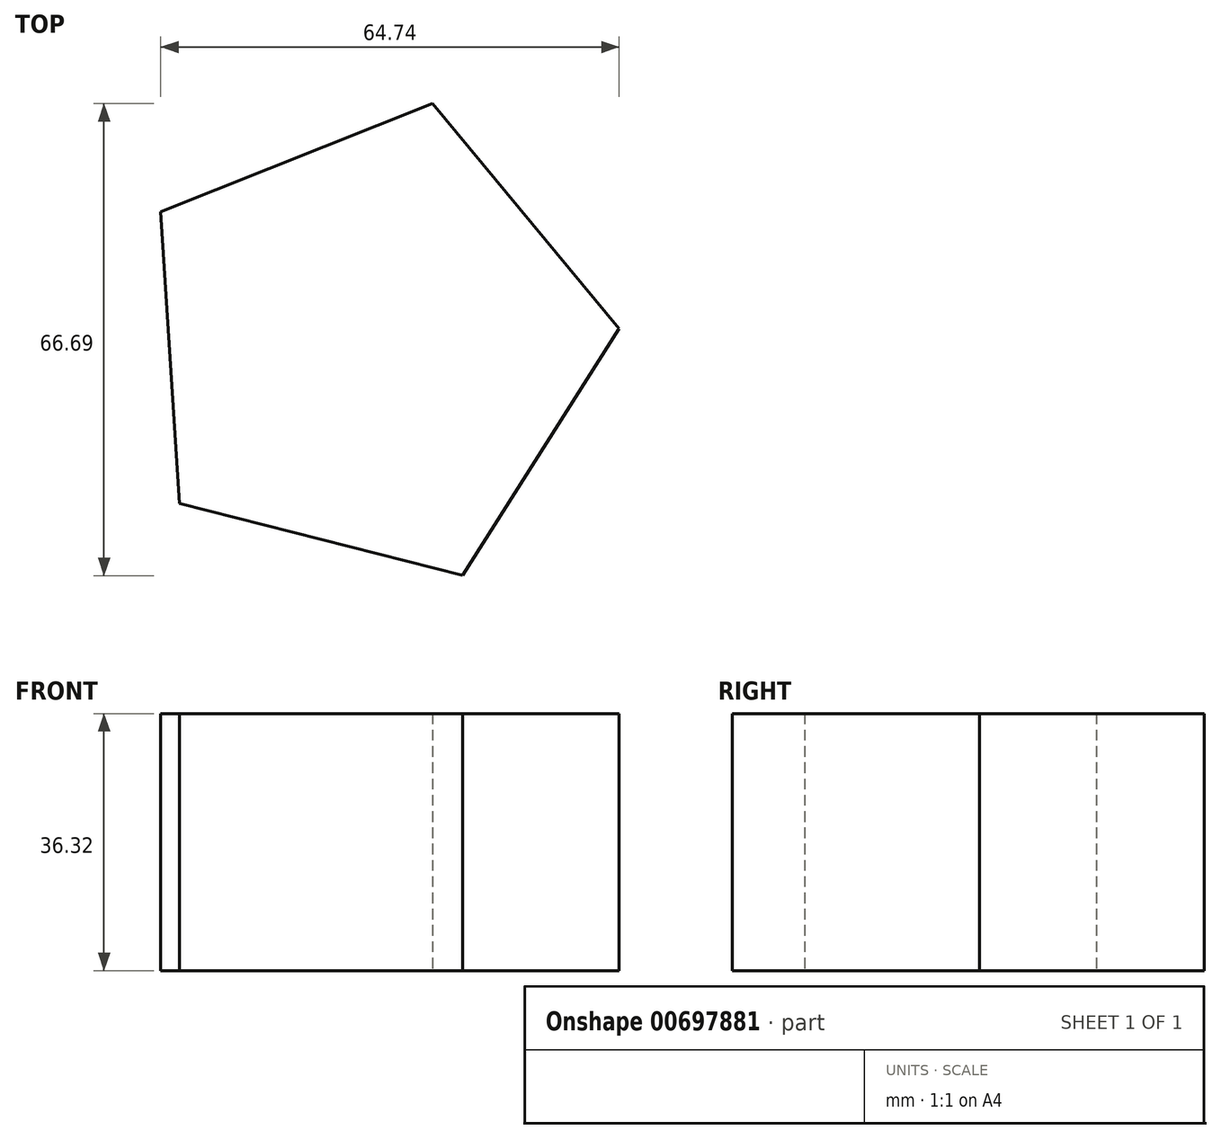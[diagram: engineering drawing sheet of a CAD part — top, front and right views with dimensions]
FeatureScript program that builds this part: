
annotation { "Feature Type Name" : "Feature", "Feature Type Description" : "" }
export const myFeature = defineFeature(function(context is Context, id is Id, definition is map)
    precondition{}
    {
        {
            var Q0;
            Q0=qCreatedBy(makeId("Top.planeOp"),FACE);
            var sketch = newSketch(context, id + "F0", { "sketchPlane" : qUnion([Q0])});
            skCircle(sketch, "E0.cCircle", {"center": v(-21.28, 21.64) * mm, "radius": 28.42 * mm, "construction": true});
            skLineSegment(sketch, "E0.0", {"start": v(13.77, 23.9) * mm, "end": v(-8.3, -11) * mm});
            skLineSegment(sketch, "E0.1", {"start": v(-8.3, -11) * mm, "end": v(-48.31, -0.8) * mm});
            skLineSegment(sketch, "E0.2", {"start": v(-48.31, -0.8) * mm, "end": v(-50.97, 40.41) * mm});
            skLineSegment(sketch, "E0.3", {"start": v(-50.97, 40.41) * mm, "end": v(-12.6, 55.68) * mm});
            skLineSegment(sketch, "E0.4", {"start": v(-12.6, 55.68) * mm, "end": v(13.77, 23.9) * mm});
            skPoint(sketch, "E0.0.midPoint", {"position": v(2.74, 6.45) * mm});
            skSolve(sketch);
        }
        {
            var Q0;
            Q0 = qSketchRegion(id + "F0", true);
            extrude(context, id + "F1", {"entities" : qUnion([Q0]), "depth" : 36.32 * mm, "offsetDistance" : 25.4 * mm});
        }
    });
